# Revit family: result
name_source: partatom
category: Mechanical Equipment
units: mm (PartAtom-declared; Revit-internal decimal feet)

## family parameters
Always vertical = No
Cut with Voids When Loaded = No
Maintain Annotation Orientation = No
OmniClass Number = 23.75.10.00
OmniClass Title = Transformation and Conversion of Energy
Part Type = Normal
Room Calculation Point = No
Round Connector Dimension = Use Radius
Shared = No
Work Plane-Based = No

## types (1)
- 2760-SABIK-350
    AUX.1 = 145 mm
    AUX.1.1 = 149 mm
    AUX.2 = 145 mm
    AUX.2.1 = 149 mm
    AUX.3 = 145 mm
    AUX.3.1 = 149 mm
    AUX.4 = 145 mm
    AUX.4.1 = 149 mm
    AUX.A = 350 mm  [stored 1.14829 ft]
    Autor = BIM6D
    CorrienteNominal = 0 A
    Default Elevation = 0 mm  [stored 0 ft]
    DiametroImpulsor = 0 mm  [stored 0 ft]
    IfcExportAs = IfcAirToAirHeatRecoveryType
    IfcExportType = FIXEDPLATECROSSFLOWEXCHANGER
    IndiceFlujoNominal = 0.0 L/s
    IndicePotenciaNominal = 0 W
    Manufacturer = S&P Sistemas de Ventilación S.L.U.
    MasterformatCodigo = 23 72 00
    MasterformatTitulo = Air-to-Air Energy Recovery Equipment
    Material Carcasa = SP_Plastic_Beige
    Material Conector Bornes = SP_Plastic_Beige
    NumeroPolos = 1
    OmniclassCodigo = 23.75.10.00
    OmniclassTitulo = Transformation and Conversion of Energy
    PA = 700 mm  [stored 2.29659 ft]
    PB = 1046 mm  [stored 3.43176 ft]
    PC = 603 mm
    PD1 = 150 mm
    PD2 = 150 mm
    PD3 = 150 mm
    PD4 = 150 mm
    PE = 248 mm  [stored 0.813648 ft]
    PF = 160 mm  [stored 0.524934 ft]
    PG = 235 mm  [stored 0.770997 ft]
    PH = 111 mm
    PII = 196 mm  [stored 0.643045 ft]
    PJ = 300 mm
    PK = 414 mm  [stored 1.35827 ft]
    PL = 440 mm  [stored 1.44357 ft]
    PM = 273 mm  [stored 0.895669 ft]
    PN = 21 mm  [stored 0.0688976 ft]
    PO = 19 mm  [stored 0.062336 ft]
    PesoBruto = 0.00 kg
    PowerFactor = 0.00%
    PresionDinamica = 0.0 Pa
    PresionEstaticaNominal = 0.0 Pa
    PresionTotalNominal = 0.0 Pa
    Radius Connector  2 = 75 mm
    Radius Connector  4 = 75 mm
    Radius Connector 1 = 75 mm
    Radius Connector 3 = 75 mm
    Radius Connector Drain = 10 mm  [stored 0.0328084 ft]
    TensionNominal = 0 V
    Type Image = <None>
    UNSPSCCodigo = 72151204
    UNSPSCTitulo = HVAC ventilation and duct work construction service
    URL = https://www.solerpalau.com
    URLProducto = https://www.solerpalau.com
    Uniclass2.0Codigo = Pr_60_60_36
    Uniclass2.0Titulo = Heat recovery distribution equipment
    spIntensidadMaximaAbsorbida = 0 A
    spPotenciaElectrica_Solucion = 0 W
    spPotenciaUtil_Solucion = 0 W
    spTamañoVentilador = 0 mm  [stored 0 ft]

note: [stored X ft] marks values corroborated as IEEE doubles in the binary element streams (Revit-internal decimal feet)
